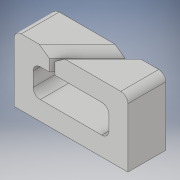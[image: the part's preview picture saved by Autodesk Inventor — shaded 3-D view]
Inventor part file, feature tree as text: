
AUTODESK INVENTOR PART (.ipt)
format: ipt  version: 2019 (Build 230136000, 136)  size: 142,336 bytes
history: native  units: mm
features: extrude x2, sketch x2, chamfer x1, fillet x1
ambient origin geometry x8: Origin, YZ Plane, XZ Plane, XY Plane, X Axis, Y Axis, Z Axis, Center Point
bodies: Solid1 (feature_tree)
feature tree (6):
  extrude  "Extrusion1"  Depth=2.0mm
  extrude  "Extrusion2"  Depth=0.75mm
  chamfer  "Chamfer1"  Distance=2.0mm
  fillet  "Fillet1"  Radius=1.25mm
  sketch  "Sketch1"  dims[d0=2.0mm d1=2.5mm]
  sketch  "Sketch2"  dims[d2=2.5mm d3=1.25mm d4=2.0mm d5=1.25mm d6=1.0mm d7=3.0mm d8=8.0mm d9=2.0mm d10=4.0mm d11=0.0mm d12=2.0mm d13=2.0mm d15=0.3mm d16=0.3mm d17=4.0mm d18=0.0mm d19=0.75mm d20=2.0mm d21=45.0deg d22=0.75mm d23=0.75mm]
